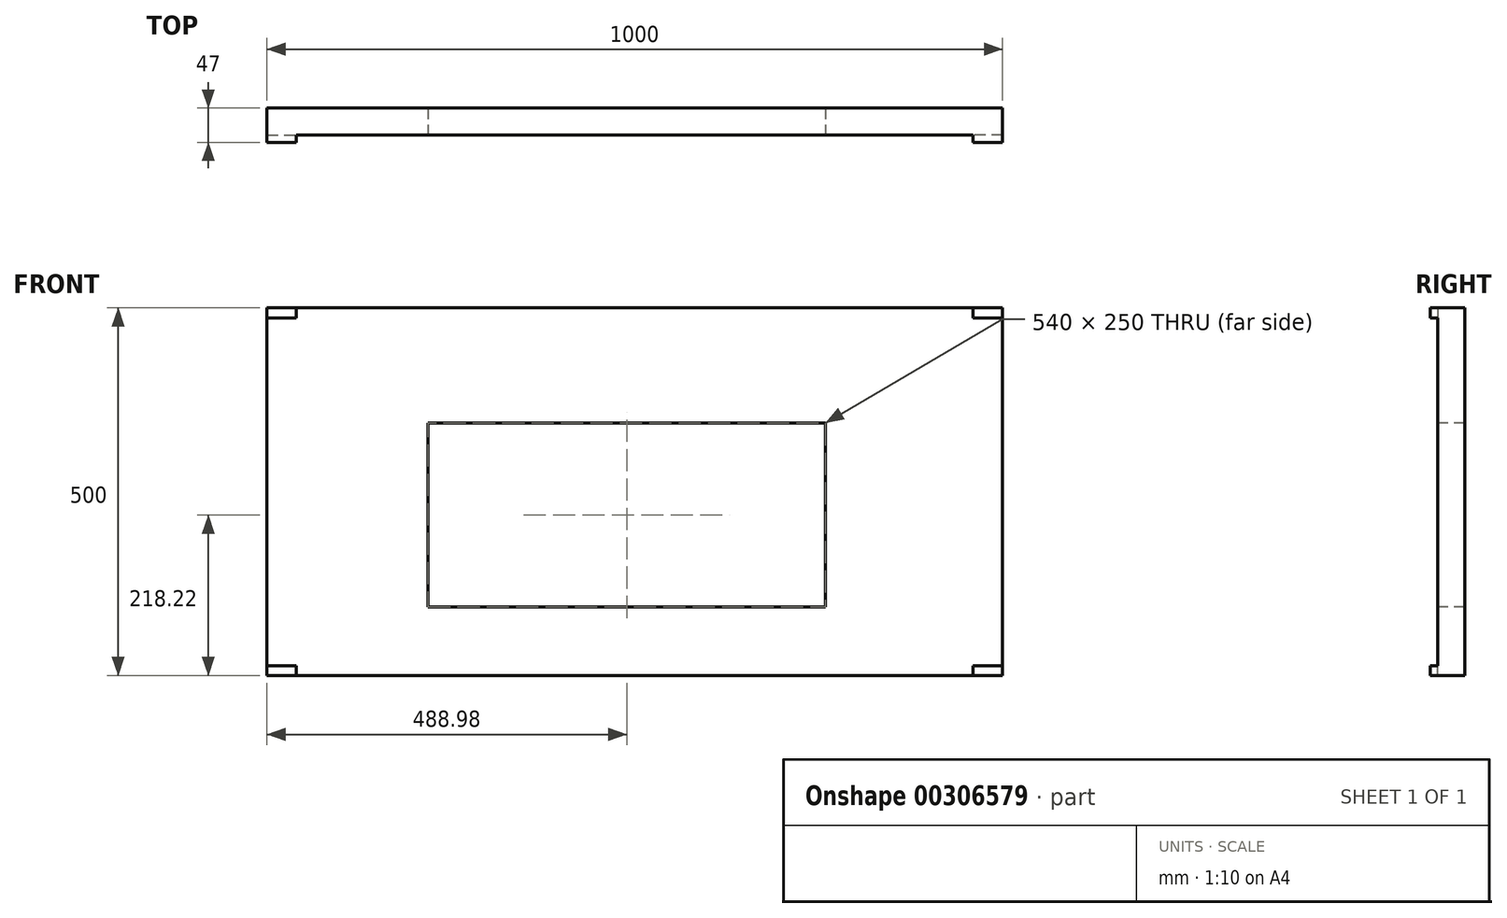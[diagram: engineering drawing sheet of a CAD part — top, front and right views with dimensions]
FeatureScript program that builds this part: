
annotation { "Feature Type Name" : "Feature", "Feature Type Description" : "" }
export const myFeature = defineFeature(function(context is Context, id is Id, definition is map)
    precondition{}
    {
        {
            var Q0;
            Q0=qCreatedBy(makeId("Front.planeOp"),FACE);
            var sketch = newSketch(context, id + "F0", { "sketchPlane" : qUnion([Q0])});
            skLineSegment(sketch, "E0.bottom", {"start": v(-97.8, 56.36) * mm, "end": v(102.2, 56.36) * mm});
            skLineSegment(sketch, "E0.top", {"start": v(-97.8, -43.64) * mm, "end": v(102.2, -43.64) * mm});
            skLineSegment(sketch, "E0.left", {"start": v(-97.8, 56.36) * mm, "end": v(-97.8, -43.64) * mm});
            skLineSegment(sketch, "E0.right", {"start": v(102.2, 56.36) * mm, "end": v(102.2, -43.64) * mm});
            skSolve(sketch);
        }
        {
            var Q0;
            Q0=makeQuery(id+"F0.imprint","IMPRINT",FACE,{"disambiguationData":[TD([[makeQuery(id+"F0.imprint","IMPRINT",EDGE,{"derivedFrom":sQuery(id+"F0.wireOp",EDGE,"E0.bottom")}),-1.0]])]});
            extrude(context, id + "F1", {"entities" : qUnion([Q0]), "depth" : 7.4 * mm});
        }
        {
            var Q0;
            Q0=makeQuery(id+"F1.opExtrude","CAP_FACE",FACE,{"disambiguationData":[OSD([sQuery(id+"F0.wireOp",EDGE,"E0.bottom"),sQuery(id+"F0.wireOp",EDGE,"E0.top"),sQuery(id+"F0.wireOp",EDGE,"E0.left"),sQuery(id+"F0.wireOp",EDGE,"E0.right")])],"isStart":false});
            var sketch = newSketch(context, id + "F2", { "sketchPlane" : qUnion([Q0])});
            skLineSegment(sketch, "E1.bottom", {"start": v(-97.8, 56.36) * mm, "end": v(-89.8, 56.36) * mm});
            skLineSegment(sketch, "E1.top", {"start": v(-97.8, 53.66) * mm, "end": v(-89.8, 53.66) * mm});
            skLineSegment(sketch, "E1.left", {"start": v(-97.8, 56.36) * mm, "end": v(-97.8, 53.66) * mm});
            skLineSegment(sketch, "E1.right", {"start": v(-89.8, 56.36) * mm, "end": v(-89.8, 53.66) * mm});
            skLineSegment(sketch, "E2.bottom", {"start": v(102.2, 56.36) * mm, "end": v(94.2, 56.36) * mm});
            skLineSegment(sketch, "E2.top", {"start": v(102.2, 53.66) * mm, "end": v(94.2, 53.66) * mm});
            skLineSegment(sketch, "E2.left", {"start": v(102.2, 56.36) * mm, "end": v(102.2, 53.66) * mm});
            skLineSegment(sketch, "E2.right", {"start": v(94.2, 56.36) * mm, "end": v(94.2, 53.66) * mm});
            skLineSegment(sketch, "E3.bottom", {"start": v(-97.8, -43.64) * mm, "end": v(-89.8, -43.64) * mm});
            skLineSegment(sketch, "E3.top", {"start": v(-97.8, -40.94) * mm, "end": v(-89.8, -40.94) * mm});
            skLineSegment(sketch, "E3.left", {"start": v(-97.8, -43.64) * mm, "end": v(-97.8, -40.94) * mm});
            skLineSegment(sketch, "E3.right", {"start": v(-89.8, -43.64) * mm, "end": v(-89.8, -40.94) * mm});
            skLineSegment(sketch, "E4.bottom", {"start": v(102.2, -43.64) * mm, "end": v(94.2, -43.64) * mm});
            skLineSegment(sketch, "E4.top", {"start": v(102.2, -40.94) * mm, "end": v(94.2, -40.94) * mm});
            skLineSegment(sketch, "E4.left", {"start": v(102.2, -43.64) * mm, "end": v(102.2, -40.94) * mm});
            skLineSegment(sketch, "E4.right", {"start": v(94.2, -43.64) * mm, "end": v(94.2, -40.94) * mm});
            skSolve(sketch);
        }
        {
            var Q0;
            Q0=makeQuery(id+"F2.imprint","IMPRINT",FACE,{"disambiguationData":[TD([[makeQuery(id+"F2.imprint","IMPRINT",EDGE,{"derivedFrom":sQuery(id+"F2.wireOp",EDGE,"E1.bottom")}),-1.0]])]});
            var Q1;
            Q1=makeQuery(id+"F2.imprint","IMPRINT",FACE,{"disambiguationData":[TD([[makeQuery(id+"F2.imprint","IMPRINT",EDGE,{"derivedFrom":sQuery(id+"F2.wireOp",EDGE,"E2.bottom")}),-1.0]])]});
            var Q2;
            Q2=makeQuery(id+"F2.imprint","IMPRINT",FACE,{"disambiguationData":[TD([[makeQuery(id+"F2.imprint","IMPRINT",EDGE,{"derivedFrom":sQuery(id+"F2.wireOp",EDGE,"E4.bottom")}),1.0]])]});
            var Q3;
            Q3=makeQuery(id+"F2.imprint","IMPRINT",FACE,{"disambiguationData":[TD([[makeQuery(id+"F2.imprint","IMPRINT",EDGE,{"derivedFrom":sQuery(id+"F2.wireOp",EDGE,"E3.bottom")}),1.0]])]});
            extrude(context, id + "F3", {"entities" : qUnion([Q0, Q1, Q2, Q3]), "operationType" : NewBodyOperationType.ADD, "depth" : 2 * mm});
        }
        {
            var Q0;
            Q0=makeQuery(id+"F1.opExtrude","CAP_FACE",FACE,{"disambiguationData":[OSD([sQuery(id+"F0.wireOp",EDGE,"E0.bottom"),sQuery(id+"F0.wireOp",EDGE,"E0.top"),sQuery(id+"F0.wireOp",EDGE,"E0.left"),sQuery(id+"F0.wireOp",EDGE,"E0.right")])],"isStart":false});
            var sketch = newSketch(context, id + "F4", { "sketchPlane" : qUnion([Q0])});
            skLineSegment(sketch, "E5.bottom", {"start": v(-54, 25) * mm, "end": v(54, 25) * mm});
            skLineSegment(sketch, "E5.top", {"start": v(-54, -25) * mm, "end": v(54, -25) * mm});
            skLineSegment(sketch, "E5.left", {"start": v(-54, 25) * mm, "end": v(-54, -25) * mm});
            skLineSegment(sketch, "E5.right", {"start": v(54, 25) * mm, "end": v(54, -25) * mm});
            skPoint(sketch, "E5.middle", {"position": v(0, 0) * mm});
            skSolve(sketch);
        }
        {
            var Q0;
            Q0=makeQuery(id+"F4.imprint","IMPRINT",FACE,{"disambiguationData":[TD([[makeQuery(id+"F4.imprint","IMPRINT",EDGE,{"derivedFrom":sQuery(id+"F4.wireOp",EDGE,"E5.bottom")}),-1.0]])]});
            extrude(context, id + "F5", {"entities" : qUnion([Q0]), "operationType" : NewBodyOperationType.REMOVE, "endBound" : BoundingType.THROUGH_ALL, "oppositeDirection" : true, "depth" : 25 * mm});
        }
        {
            var Q0;
            Q0=makeQuery(id+"F1.opExtrude","SWEPT_BODY",BODY,{"disambiguationData":[OSD([sQuery(id+"F0.wireOp",EDGE,"E0.bottom"),sQuery(id+"F0.wireOp",EDGE,"E0.top"),sQuery(id+"F0.wireOp",EDGE,"E0.left"),sQuery(id+"F0.wireOp",EDGE,"E0.right")])]});
            var Q1;
            Q1=qCreatedBy(makeId("Origin.pointOp"),VERTEX);
            transform(context, id + "F6", {"entities" : qUnion([Q0]), "transformType" : TransformType.SCALE_UNIFORMLY, "scale" : 5, "scalePoint" : qUnion([Q1]), "makeCopy" : false});
        }
    });
